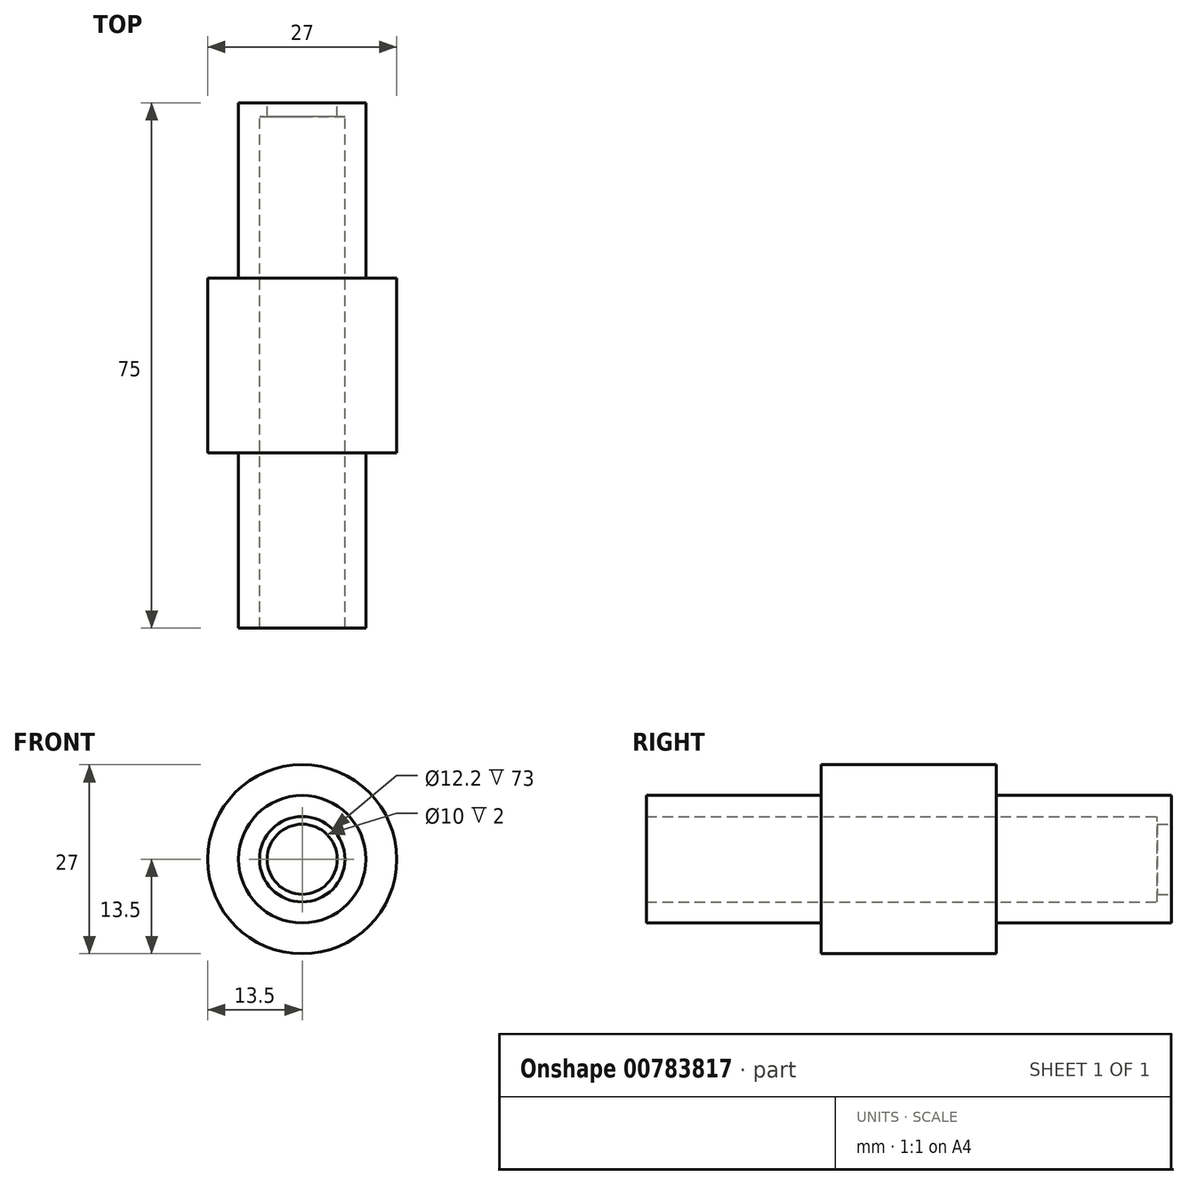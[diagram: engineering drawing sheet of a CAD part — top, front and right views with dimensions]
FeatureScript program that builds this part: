
annotation { "Feature Type Name" : "Feature", "Feature Type Description" : "" }
export const myFeature = defineFeature(function(context is Context, id is Id, definition is map)
    precondition{}
    {
        {
            var Q0;
            Q0=qCreatedBy(makeId("Front.planeOp"),FACE);
            var sketch = newSketch(context, id + "F0", { "sketchPlane" : qUnion([Q0])});
            skCircle(sketch, "E0", {"center": v(0, 0) * mm, "radius": 6.1 * mm});
            skCircle(sketch, "E1", {"center": v(0, 0) * mm, "radius": 9.1 * mm});
            skSolve(sketch);
        }
        {
            var Q0;
            Q0=makeQuery(id+"F0.imprint","IMPRINT",FACE,{"disambiguationData":[TD([[makeQuery(id+"F0.imprint","IMPRINT",EDGE,{"derivedFrom":sQuery(id+"F0.wireOp",EDGE,"E0")}),-1.0]])]});
            extrude(context, id + "F1", {"entities" : qUnion([Q0]), "depth" : 25 * mm, "offsetDistance" : 25 * mm});
        }
        {
            var Q0;
            Q0=makeQuery(id+"F1.opExtrude","CAP_FACE",FACE,{"disambiguationData":[OSD([sQuery(id+"F0.wireOp",EDGE,"E0"),sQuery(id+"F0.wireOp",EDGE,"E1")])],"isStart":false});
            var sketch = newSketch(context, id + "F2", { "sketchPlane" : qUnion([Q0])});
            skCircle(sketch, "E2", {"center": v(0, 0) * mm, "radius": 13.5 * mm});
            skSolve(sketch);
        }
        {
            var Q0;
            Q0=makeQuery(id+"F2.imprint","IMPRINT",FACE,{"disambiguationData":[TD([[makeQuery(id+"F2.imprint","IMPRINT",EDGE,{"derivedFrom":sQuery(id+"F2.wireOp",EDGE,"E2")}),1.0]])]});
            var Q1;
            Q1=makeQuery(id+"F2.imprint","IMPRINT",FACE,{"disambiguationData":[TD([[makeQuery(id+"F2.imprint","IMPRINT",EDGE,{"derivedFrom":makeQuery(id+"F1.opExtrude","CAP_EDGE",EDGE,{"disambiguationData":[OSD([sQuery(id+"F0.wireOp",EDGE,"E0")])],"isStart":false})}),-1.0]])]});
            extrude(context, id + "F3", {"entities" : qUnion([Q0, Q1]), "operationType" : NewBodyOperationType.ADD, "depth" : 25 * mm, "offsetDistance" : 25 * mm});
        }
        {
            var Q0;
            Q0=makeQuery(id+"F3.opExtrude","CAP_FACE",FACE,{"disambiguationData":[OSD([sQuery(id+"F0.wireOp",EDGE,"E0"),sQuery(id+"F2.wireOp",EDGE,"E2")])],"isStart":false});
            var sketch = newSketch(context, id + "F4", { "sketchPlane" : qUnion([Q0])});
            skCircle(sketch, "E3.0", {"center": v(0, 0) * mm, "radius": 9.1 * mm});
            skCircle(sketch, "E4.0", {"center": v(0, 0) * mm, "radius": 6.1 * mm});
            skSolve(sketch);
        }
        {
            var Q0;
            Q0=makeQuery(id+"F4.imprint","IMPRINT",FACE,{"disambiguationData":[TD([[makeQuery(id+"F4.imprint","IMPRINT",EDGE,{"derivedFrom":sQuery(id+"F4.wireOp",EDGE,"E3.0")}),1.0]])]});
            extrude(context, id + "F5", {"entities" : qUnion([Q0]), "operationType" : NewBodyOperationType.ADD, "depth" : 25 * mm, "offsetDistance" : 25 * mm});
        }
        {
            var Q0;
            Q0=makeQuery(id+"F1.opExtrude","CAP_FACE",FACE,{"disambiguationData":[OSD([sQuery(id+"F0.wireOp",EDGE,"E0"),sQuery(id+"F0.wireOp",EDGE,"E1")])],"isStart":true});
            var sketch = newSketch(context, id + "F6", { "sketchPlane" : qUnion([Q0])});
            skCircle(sketch, "E5", {"center": v(0, 0) * mm, "radius": 5 * mm});
            skSolve(sketch);
        }
        {
            var Q0;
            Q0=makeQuery(id+"F6.imprint","IMPRINT",FACE,{"disambiguationData":[TD([[makeQuery(id+"F6.imprint","IMPRINT",EDGE,{"derivedFrom":sQuery(id+"F6.wireOp",EDGE,"E5")}),-1.0]])]});
            extrude(context, id + "F7", {"entities" : qUnion([Q0]), "operationType" : NewBodyOperationType.ADD, "oppositeDirection" : true, "depth" : 2 * mm, "offsetDistance" : 25 * mm});
        }
    });
